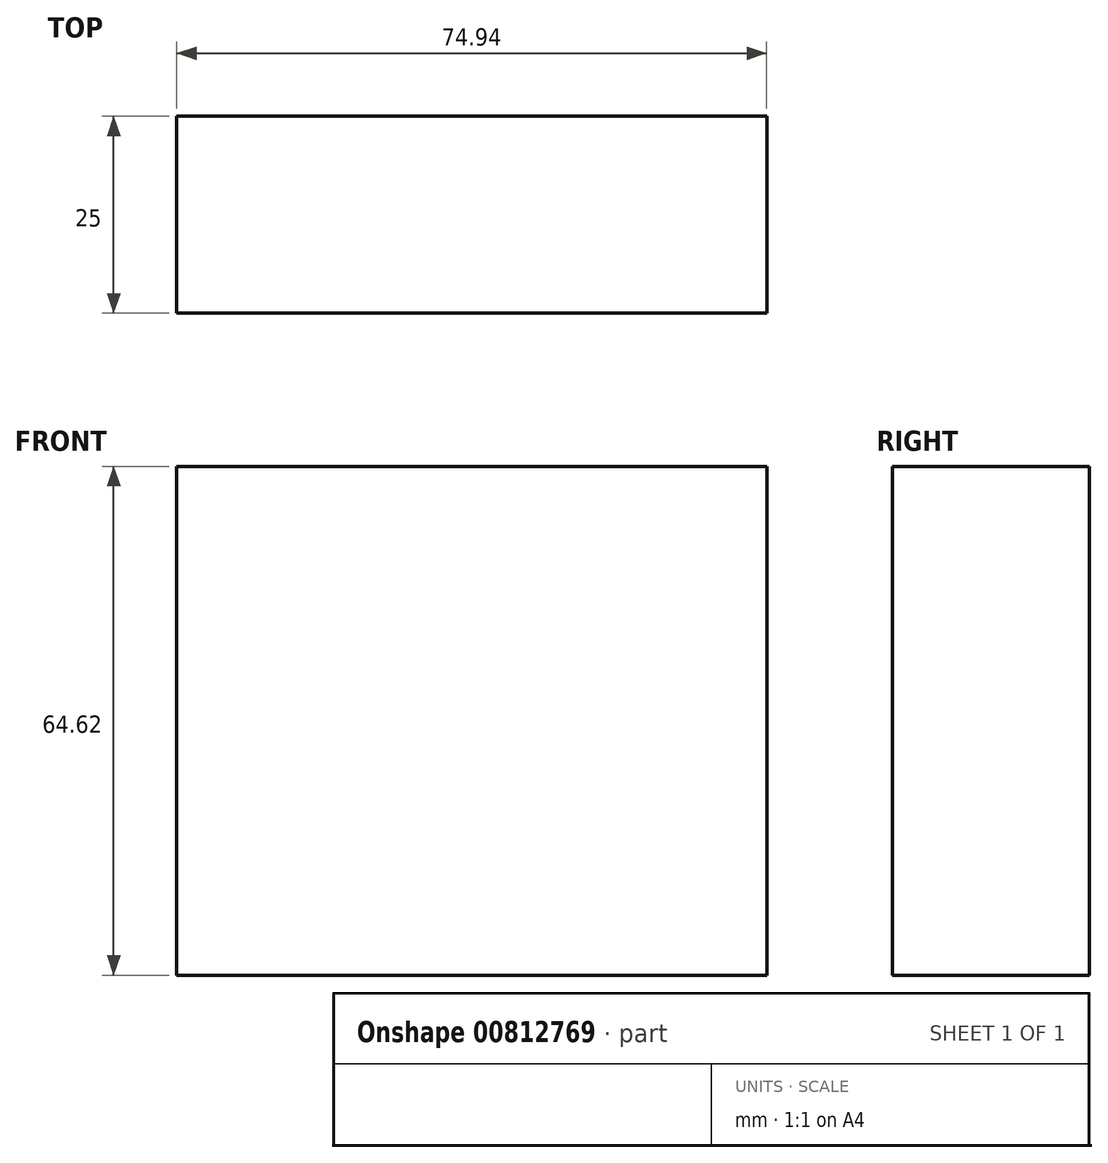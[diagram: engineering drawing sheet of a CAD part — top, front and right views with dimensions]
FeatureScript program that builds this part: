
annotation { "Feature Type Name" : "Feature", "Feature Type Description" : "" }
export const myFeature = defineFeature(function(context is Context, id is Id, definition is map)
    precondition{}
    {
        {
            var Q0;
            Q0=qCreatedBy(makeId("Front.planeOp"),FACE);
            var sketch = newSketch(context, id + "F0", { "sketchPlane" : qUnion([Q0])});
            skLineSegment(sketch, "E0.bottom", {"start": v(37.47, 33.8) * mm, "end": v(-37.47, 33.8) * mm});
            skLineSegment(sketch, "E0.top", {"start": v(37.47, -33.8) * mm, "end": v(-37.47, -33.8) * mm});
            skLineSegment(sketch, "E0.left", {"start": v(37.47, 33.8) * mm, "end": v(37.47, -33.8) * mm});
            skLineSegment(sketch, "E0.right", {"start": v(-37.47, 33.8) * mm, "end": v(-37.47, -33.8) * mm});
            skPoint(sketch, "E0.middle", {"position": v(0, 0) * mm});
            skSolve(sketch);
        }
        {
            var Q0;
            Q0=makeQuery(id+"F0.imprint","IMPRINT",FACE,{"disambiguationData":[TD([[makeQuery(id+"F0.imprint","IMPRINT",EDGE,{"derivedFrom":sQuery(id+"F0.wireOp",EDGE,"E0.bottom")}),1.0]])]});
            var Q1;
            Q1=sQuery(id+"F0.wireOp",EDGE,"E0.right");
            var Q2;
            Q2=sQuery(id+"F0.wireOp",EDGE,"E0.top");
            var Q3;
            Q3=sQuery(id+"F0.wireOp",EDGE,"E0.left");
            var Q4;
            Q4=sQuery(id+"F0.wireOp",EDGE,"E0.bottom");
            extrude(context, id + "F1", {"entities" : qUnion([Q0]), "surfaceEntities" : qUnion([Q1, Q2, Q3, Q4]), "endBound" : BoundingType.SYMMETRIC, "depth" : 25 * mm, "offsetDistance" : 25.4 * mm});
        }
        {
            var Q0;
            Q0=makeQuery(id+"F1.opExtrude","SWEPT_FACE",FACE,{"disambiguationData":[OSD([sQuery(id+"F0.wireOp",EDGE,"E0.bottom")])]});
            extrude(context, id + "F2", {"entities" : qUnion([Q0]), "operationType" : NewBodyOperationType.REMOVE, "oppositeDirection" : true, "depth" : 3 * mm, "offsetDistance" : 25.4 * mm});
        }
    });
